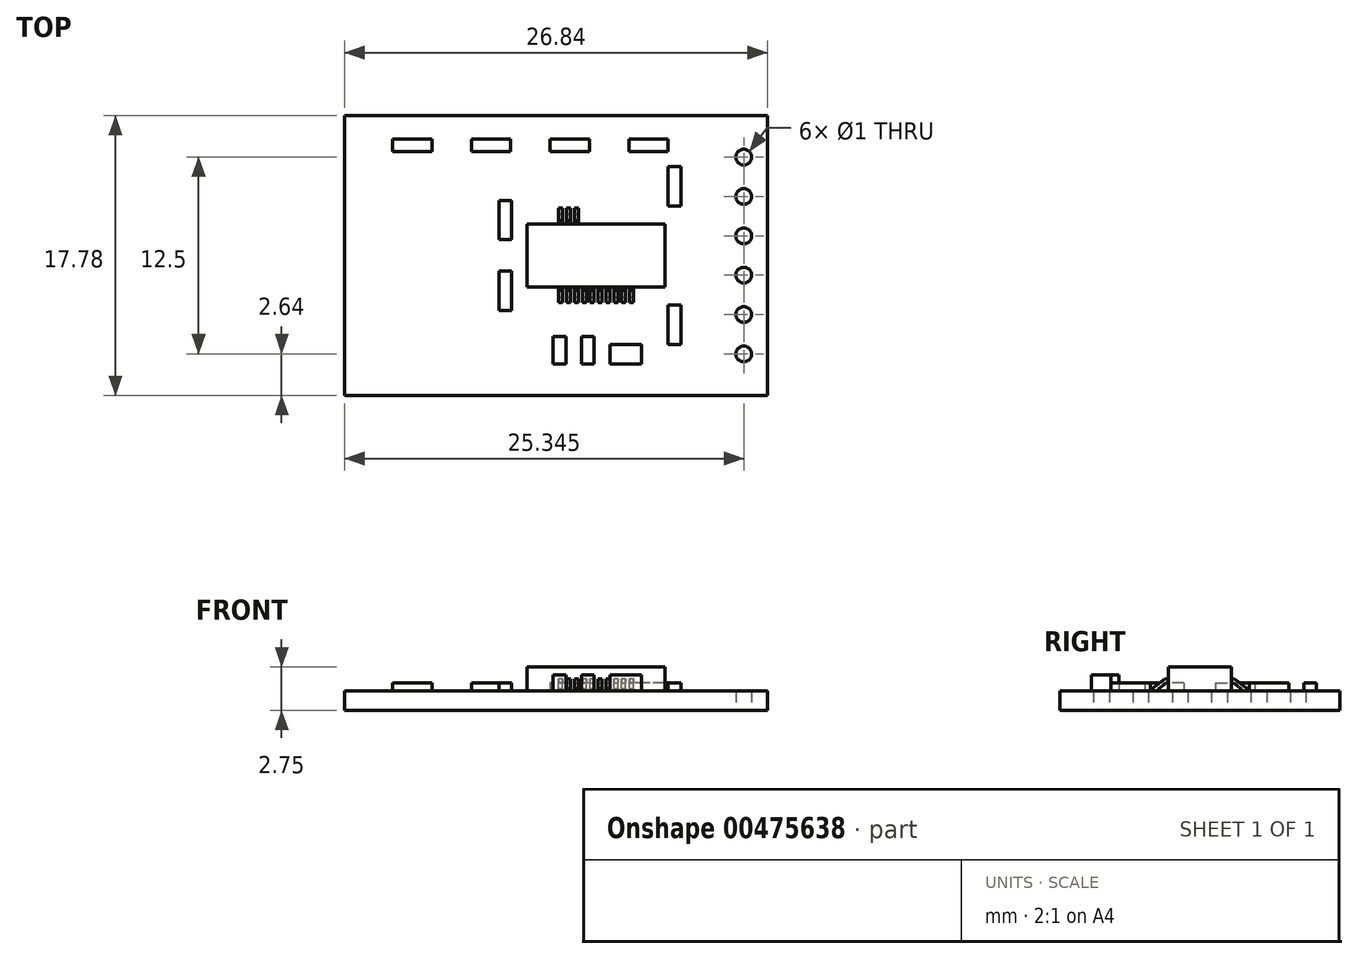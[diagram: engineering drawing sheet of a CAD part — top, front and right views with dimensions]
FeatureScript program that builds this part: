
annotation { "Feature Type Name" : "Feature", "Feature Type Description" : "" }
export const myFeature = defineFeature(function(context is Context, id is Id, definition is map)
    precondition{}
    {
        {
            var Q0;
            Q0=qCreatedBy(makeId("Top.planeOp"),FACE);
            var sketch = newSketch(context, id + "F0", { "sketchPlane" : qUnion([Q0])});
            skLineSegment(sketch, "E0.bottom", {"start": v(13.43, -8.9) * mm, "end": v(-13.42, -8.9) * mm});
            skLineSegment(sketch, "E0.top", {"start": v(13.42, 8.9) * mm, "end": v(-13.43, 8.9) * mm});
            skLineSegment(sketch, "E0.left", {"start": v(13.43, -8.9) * mm, "end": v(13.42, 8.9) * mm});
            skLineSegment(sketch, "E0.right", {"start": v(-13.42, -8.9) * mm, "end": v(-13.43, 8.9) * mm});
            skPoint(sketch, "E0.middle", {"position": v(0, 0) * mm});
            skCircle(sketch, "E1", {"center": v(11.92, 6.25) * mm, "radius": 0.5 * mm});
            skCircle(sketch, "E2.1.0.0", {"center": v(11.92, 3.75) * mm, "radius": 0.5 * mm});
            skCircle(sketch, "E2.2.0.0", {"center": v(11.92, 1.25) * mm, "radius": 0.5 * mm});
            skCircle(sketch, "E2.3.0.0", {"center": v(11.92, -1.25) * mm, "radius": 0.5 * mm});
            skCircle(sketch, "E2.4.0.0", {"center": v(11.92, -3.75) * mm, "radius": 0.5 * mm});
            skCircle(sketch, "E2.5.0.0", {"center": v(11.92, -6.25) * mm, "radius": 0.5 * mm});
            skLineSegment(sketch, "E2.direction1", {"start": v(11.92, 6.25) * mm, "end": v(11.92, 3.75) * mm, "construction": true});
            skLineSegment(sketch, "E3", {"start": v(11.92, 1.25) * mm, "end": v(11.92, -1.25) * mm, "construction": true});
            skPoint(sketch, "E4", {"position": v(11.92, 0) * mm});
            skPoint(sketch, "E5", {"position": v(13.42, 0) * mm});
            skSolve(sketch);
        }
        {
            var Q0;
            Q0 = qSketchRegion(id + "F0", true);
            extrude(context, id + "F1", {"entities" : qUnion([Q0]), "depth" : 1.25 * mm});
        }
        {
            var Q0;
            Q0=makeQuery(id+"F1.opExtrude","CAP_FACE",FACE,{"disambiguationData":[OSD([sQuery(id+"F0.wireOp",EDGE,"E0.bottom"),sQuery(id+"F0.wireOp",EDGE,"E0.top"),sQuery(id+"F0.wireOp",EDGE,"E0.left"),sQuery(id+"F0.wireOp",EDGE,"E0.right"),sQuery(id+"F0.wireOp",EDGE,"E1"),sQuery(id+"F0.wireOp",EDGE,"E2.1.0.0"),sQuery(id+"F0.wireOp",EDGE,"E2.2.0.0"),sQuery(id+"F0.wireOp",EDGE,"E2.3.0.0"),sQuery(id+"F0.wireOp",EDGE,"E2.4.0.0"),sQuery(id+"F0.wireOp",EDGE,"E2.5.0.0")])],"isStart":false});
            var sketch = newSketch(context, id + "F2", { "sketchPlane" : qUnion([Q0])});
            skLineSegment(sketch, "E6.bottom", {"start": v(6.92, -2) * mm, "end": v(-1.83, -2) * mm});
            skLineSegment(sketch, "E6.top", {"start": v(6.92, 2) * mm, "end": v(-1.83, 2) * mm});
            skLineSegment(sketch, "E6.left", {"start": v(6.92, -2) * mm, "end": v(6.92, 2) * mm});
            skLineSegment(sketch, "E6.right", {"start": v(-1.83, -2) * mm, "end": v(-1.83, 2) * mm});
            skPoint(sketch, "E6.middle", {"position": v(2.55, 0) * mm});
            skLineSegment(sketch, "E7.bottom", {"start": v(0.42, -3) * mm, "end": v(0.17, -3) * mm});
            skLineSegment(sketch, "E7.top", {"start": v(0.42, -2) * mm, "end": v(0.17, -2) * mm});
            skLineSegment(sketch, "E7.left", {"start": v(0.42, -3) * mm, "end": v(0.42, -2) * mm});
            skLineSegment(sketch, "E7.right", {"start": v(0.17, -3) * mm, "end": v(0.17, -2) * mm});
            skPoint(sketch, "E7.middle", {"position": v(0.3, -2.5) * mm});
            skPoint(sketch, "E8.1.0.0", {"position": v(0.8, -2.5) * mm});
            skLineSegment(sketch, "E8.1.0.1", {"start": v(0.92, -3) * mm, "end": v(0.67, -3) * mm});
            skLineSegment(sketch, "E8.1.0.2", {"start": v(0.92, -2) * mm, "end": v(0.67, -2) * mm});
            skLineSegment(sketch, "E8.1.0.3", {"start": v(0.92, -3) * mm, "end": v(0.92, -2) * mm});
            skLineSegment(sketch, "E8.1.0.4", {"start": v(0.67, -3) * mm, "end": v(0.67, -2) * mm});
            skPoint(sketch, "E8.2.0.0", {"position": v(1.3, -2.5) * mm});
            skLineSegment(sketch, "E8.2.0.1", {"start": v(1.42, -3) * mm, "end": v(1.17, -3) * mm});
            skLineSegment(sketch, "E8.2.0.2", {"start": v(1.42, -2) * mm, "end": v(1.17, -2) * mm});
            skLineSegment(sketch, "E8.2.0.3", {"start": v(1.42, -3) * mm, "end": v(1.42, -2) * mm});
            skLineSegment(sketch, "E8.2.0.4", {"start": v(1.17, -3) * mm, "end": v(1.17, -2) * mm});
            skPoint(sketch, "E8.3.0.0", {"position": v(1.8, -2.5) * mm});
            skLineSegment(sketch, "E8.3.0.1", {"start": v(1.92, -3) * mm, "end": v(1.67, -3) * mm});
            skLineSegment(sketch, "E8.3.0.2", {"start": v(1.92, -2) * mm, "end": v(1.67, -2) * mm});
            skLineSegment(sketch, "E8.3.0.3", {"start": v(1.92, -3) * mm, "end": v(1.92, -2) * mm});
            skLineSegment(sketch, "E8.3.0.4", {"start": v(1.67, -3) * mm, "end": v(1.67, -2) * mm});
            skPoint(sketch, "E8.4.0.0", {"position": v(2.3, -2.5) * mm});
            skLineSegment(sketch, "E8.4.0.1", {"start": v(2.42, -3) * mm, "end": v(2.17, -3) * mm});
            skLineSegment(sketch, "E8.4.0.2", {"start": v(2.42, -2) * mm, "end": v(2.17, -2) * mm});
            skLineSegment(sketch, "E8.4.0.3", {"start": v(2.42, -3) * mm, "end": v(2.42, -2) * mm});
            skLineSegment(sketch, "E8.4.0.4", {"start": v(2.17, -3) * mm, "end": v(2.17, -2) * mm});
            skPoint(sketch, "E8.5.0.0", {"position": v(2.8, -2.5) * mm});
            skLineSegment(sketch, "E8.5.0.1", {"start": v(2.92, -3) * mm, "end": v(2.67, -3) * mm});
            skLineSegment(sketch, "E8.5.0.2", {"start": v(2.92, -2) * mm, "end": v(2.67, -2) * mm});
            skLineSegment(sketch, "E8.5.0.3", {"start": v(2.92, -3) * mm, "end": v(2.92, -2) * mm});
            skLineSegment(sketch, "E8.5.0.4", {"start": v(2.67, -3) * mm, "end": v(2.67, -2) * mm});
            skPoint(sketch, "E8.6.0.0", {"position": v(3.3, -2.5) * mm});
            skLineSegment(sketch, "E8.6.0.1", {"start": v(3.42, -3) * mm, "end": v(3.17, -3) * mm});
            skLineSegment(sketch, "E8.6.0.2", {"start": v(3.42, -2) * mm, "end": v(3.17, -2) * mm});
            skLineSegment(sketch, "E8.6.0.3", {"start": v(3.42, -3) * mm, "end": v(3.42, -2) * mm});
            skLineSegment(sketch, "E8.6.0.4", {"start": v(3.17, -3) * mm, "end": v(3.17, -2) * mm});
            skPoint(sketch, "E8.7.0.0", {"position": v(3.8, -2.5) * mm});
            skLineSegment(sketch, "E8.7.0.1", {"start": v(3.92, -3) * mm, "end": v(3.67, -3) * mm});
            skLineSegment(sketch, "E8.7.0.2", {"start": v(3.92, -2) * mm, "end": v(3.67, -2) * mm});
            skLineSegment(sketch, "E8.7.0.3", {"start": v(3.92, -3) * mm, "end": v(3.92, -2) * mm});
            skLineSegment(sketch, "E8.7.0.4", {"start": v(3.67, -3) * mm, "end": v(3.67, -2) * mm});
            skPoint(sketch, "E8.8.0.0", {"position": v(4.3, -2.5) * mm});
            skLineSegment(sketch, "E8.8.0.1", {"start": v(4.42, -3) * mm, "end": v(4.17, -3) * mm});
            skLineSegment(sketch, "E8.8.0.2", {"start": v(4.42, -2) * mm, "end": v(4.17, -2) * mm});
            skLineSegment(sketch, "E8.8.0.3", {"start": v(4.42, -3) * mm, "end": v(4.42, -2) * mm});
            skLineSegment(sketch, "E8.8.0.4", {"start": v(4.17, -3) * mm, "end": v(4.17, -2) * mm});
            skPoint(sketch, "E8.9.0.0", {"position": v(4.8, -2.5) * mm});
            skLineSegment(sketch, "E8.9.0.1", {"start": v(4.92, -3) * mm, "end": v(4.67, -3) * mm});
            skLineSegment(sketch, "E8.9.0.2", {"start": v(4.92, -2) * mm, "end": v(4.67, -2) * mm});
            skLineSegment(sketch, "E8.9.0.3", {"start": v(4.92, -3) * mm, "end": v(4.92, -2) * mm});
            skLineSegment(sketch, "E8.9.0.4", {"start": v(4.67, -3) * mm, "end": v(4.67, -2) * mm});
            skLineSegment(sketch, "E8.direction1", {"start": v(0.17, -3) * mm, "end": v(0.67, -3) * mm, "construction": true});
            skLineSegment(sketch, "E9", {"start": v(2.3, -2.5) * mm, "end": v(2.8, -2.5) * mm, "construction": true});
            skPoint(sketch, "E10", {"position": v(2.55, -2.5) * mm});
            skLineSegment(sketch, "E11", {"start": v(-1.83, 0) * mm, "end": v(6.92, 0) * mm, "construction": true});
            skLineSegment(sketch, "E12.MirrorCS", {"start": v(0.42, 3) * mm, "end": v(0.17, 3) * mm});
            skLineSegment(sketch, "E13.MirrorCS", {"start": v(2.92, 2) * mm, "end": v(2.67, 2) * mm});
            skLineSegment(sketch, "E14.MirrorCS", {"start": v(0.42, 2) * mm, "end": v(0.17, 2) * mm});
            skLineSegment(sketch, "E15.MirrorCS", {"start": v(4.92, 2) * mm, "end": v(4.67, 2) * mm});
            skLineSegment(sketch, "E16.MirrorCS", {"start": v(0.92, 3) * mm, "end": v(0.67, 3) * mm});
            skLineSegment(sketch, "E17.MirrorCS", {"start": v(0.92, 2) * mm, "end": v(0.67, 2) * mm});
            skLineSegment(sketch, "E18.MirrorCS", {"start": v(4.42, 2) * mm, "end": v(4.17, 2) * mm});
            skLineSegment(sketch, "E19.MirrorCS", {"start": v(1.42, 3) * mm, "end": v(1.17, 3) * mm});
            skLineSegment(sketch, "E20.MirrorCS", {"start": v(2.42, 2) * mm, "end": v(2.17, 2) * mm});
            skLineSegment(sketch, "E21.MirrorCS", {"start": v(3.92, 2) * mm, "end": v(3.67, 2) * mm});
            skLineSegment(sketch, "E22.MirrorCS", {"start": v(1.92, 2) * mm, "end": v(1.67, 2) * mm});
            skLineSegment(sketch, "E23.MirrorCS", {"start": v(3.92, 3) * mm, "end": v(3.67, 3) * mm});
            skLineSegment(sketch, "E24.MirrorCS", {"start": v(1.92, 3) * mm, "end": v(1.67, 3) * mm});
            skLineSegment(sketch, "E25.MirrorCS", {"start": v(4.42, 3) * mm, "end": v(4.17, 3) * mm});
            skLineSegment(sketch, "E26.MirrorCS", {"start": v(3.42, 2) * mm, "end": v(3.17, 2) * mm});
            skLineSegment(sketch, "E27.MirrorCS", {"start": v(2.42, 3) * mm, "end": v(2.17, 3) * mm});
            skLineSegment(sketch, "E28.MirrorCS", {"start": v(1.42, 2) * mm, "end": v(1.17, 2) * mm});
            skLineSegment(sketch, "E29.MirrorCS", {"start": v(4.92, 3) * mm, "end": v(4.67, 3) * mm});
            skLineSegment(sketch, "E30.MirrorCS", {"start": v(2.3, 2.5) * mm, "end": v(2.8, 2.5) * mm, "construction": true});
            skLineSegment(sketch, "E31.MirrorCS", {"start": v(0.17, 3) * mm, "end": v(0.67, 3) * mm, "construction": true});
            skLineSegment(sketch, "E32.MirrorCS", {"start": v(2.92, 3) * mm, "end": v(2.67, 3) * mm});
            skLineSegment(sketch, "E33.MirrorCS", {"start": v(3.42, 3) * mm, "end": v(3.17, 3) * mm});
            skLineSegment(sketch, "E34.MirrorCS", {"start": v(3.17, 3) * mm, "end": v(3.17, 2) * mm});
            skLineSegment(sketch, "E35.MirrorCS", {"start": v(4.42, 3) * mm, "end": v(4.42, 2) * mm});
            skLineSegment(sketch, "E36.MirrorCS", {"start": v(2.42, 3) * mm, "end": v(2.42, 2) * mm});
            skLineSegment(sketch, "E37.MirrorCS", {"start": v(3.67, 3) * mm, "end": v(3.67, 2) * mm});
            skLineSegment(sketch, "E38.MirrorCS", {"start": v(1.67, 3) * mm, "end": v(1.67, 2) * mm});
            skLineSegment(sketch, "E39.MirrorCS", {"start": v(0.42, 3) * mm, "end": v(0.42, 2) * mm});
            skLineSegment(sketch, "E40.MirrorCS", {"start": v(0.17, 3) * mm, "end": v(0.17, 2) * mm});
            skLineSegment(sketch, "E41.MirrorCS", {"start": v(0.92, 3) * mm, "end": v(0.92, 2) * mm});
            skLineSegment(sketch, "E42.MirrorCS", {"start": v(0.67, 3) * mm, "end": v(0.67, 2) * mm});
            skLineSegment(sketch, "E43.MirrorCS", {"start": v(3.42, 3) * mm, "end": v(3.42, 2) * mm});
            skPoint(sketch, "E44.MirrorP", {"position": v(2.8, 2.5) * mm});
            skLineSegment(sketch, "E45.MirrorCS", {"start": v(3.92, 3) * mm, "end": v(3.92, 2) * mm});
            skPoint(sketch, "E46.MirrorP", {"position": v(0.3, 2.5) * mm});
            skPoint(sketch, "E47.MirrorP", {"position": v(3.8, 2.5) * mm});
            skLineSegment(sketch, "E48.MirrorCS", {"start": v(1.92, 3) * mm, "end": v(1.92, 2) * mm});
            skPoint(sketch, "E49.MirrorP", {"position": v(4.8, 2.5) * mm});
            skPoint(sketch, "E50.MirrorP", {"position": v(1.8, 2.5) * mm});
            skPoint(sketch, "E51.MirrorP", {"position": v(2.55, 2.5) * mm});
            skLineSegment(sketch, "E52.MirrorCS", {"start": v(2.17, 3) * mm, "end": v(2.17, 2) * mm});
            skLineSegment(sketch, "E53.MirrorCS", {"start": v(2.67, 3) * mm, "end": v(2.67, 2) * mm});
            skLineSegment(sketch, "E54.MirrorCS", {"start": v(4.67, 3) * mm, "end": v(4.67, 2) * mm});
            skLineSegment(sketch, "E55.MirrorCS", {"start": v(4.17, 3) * mm, "end": v(4.17, 2) * mm});
            skPoint(sketch, "E56.MirrorP", {"position": v(2.3, 2.5) * mm});
            skPoint(sketch, "E57.MirrorP", {"position": v(3.3, 2.5) * mm});
            skPoint(sketch, "E58.MirrorP", {"position": v(0.8, 2.5) * mm});
            skLineSegment(sketch, "E59.MirrorCS", {"start": v(4.92, 3) * mm, "end": v(4.92, 2) * mm});
            skPoint(sketch, "E60.MirrorP", {"position": v(4.3, 2.5) * mm});
            skLineSegment(sketch, "E61.MirrorCS", {"start": v(2.92, 3) * mm, "end": v(2.92, 2) * mm});
            skPoint(sketch, "E62.MirrorP", {"position": v(1.3, 2.5) * mm});
            skLineSegment(sketch, "E63.MirrorCS", {"start": v(1.17, 3) * mm, "end": v(1.17, 2) * mm});
            skLineSegment(sketch, "E64.MirrorCS", {"start": v(1.42, 3) * mm, "end": v(1.42, 2) * mm});
            skSolve(sketch);
        }
        {
            var Q0;
            {var subQ13=sQuery(id+"F2.wireOp",EDGE,"E6.left");Q0=makeQuery(id+"F2.imprint","IMPRINT",FACE,{"disambiguationData":[TD([[makeQuery(id+"F2.imprint","IMPRINT",EDGE,{"derivedFrom":subQ13}),1.0]])]});}
            extrude(context, id + "F3", {"entities" : qUnion([Q0]), "depth" : 1.5 * mm});
        }
        {
            var Q0;
            Q0=makeQuery(id+"F2.imprint","IMPRINT",FACE,{"disambiguationData":[TD([[makeQuery(id+"F2.imprint","IMPRINT",EDGE,{"derivedFrom":sQuery(id+"F2.wireOp",EDGE,"E15.MirrorCS")}),-1.0]])]});
            var Q1;
            Q1=makeQuery(id+"F2.imprint","IMPRINT",FACE,{"disambiguationData":[TD([[makeQuery(id+"F2.imprint","IMPRINT",EDGE,{"derivedFrom":sQuery(id+"F2.wireOp",EDGE,"E22.MirrorCS")}),-1.0]])]});
            var Q2;
            Q2=makeQuery(id+"F2.imprint","IMPRINT",FACE,{"disambiguationData":[TD([[makeQuery(id+"F2.imprint","IMPRINT",EDGE,{"derivedFrom":sQuery(id+"F2.wireOp",EDGE,"E18.MirrorCS")}),-1.0]])]});
            var Q3;
            Q3=makeQuery(id+"F2.imprint","IMPRINT",FACE,{"disambiguationData":[TD([[makeQuery(id+"F2.imprint","IMPRINT",EDGE,{"derivedFrom":sQuery(id+"F2.wireOp",EDGE,"E8.8.0.1")}),-1.0]])]});
            var Q4;
            Q4=makeQuery(id+"F2.imprint","IMPRINT",FACE,{"disambiguationData":[TD([[makeQuery(id+"F2.imprint","IMPRINT",EDGE,{"derivedFrom":sQuery(id+"F2.wireOp",EDGE,"E13.MirrorCS")}),-1.0]])]});
            var Q5;
            Q5=makeQuery(id+"F2.imprint","IMPRINT",FACE,{"disambiguationData":[TD([[makeQuery(id+"F2.imprint","IMPRINT",EDGE,{"derivedFrom":sQuery(id+"F2.wireOp",EDGE,"E19.MirrorCS")}),1.0]])]});
            var Q6;
            Q6=makeQuery(id+"F2.imprint","IMPRINT",FACE,{"disambiguationData":[TD([[makeQuery(id+"F2.imprint","IMPRINT",EDGE,{"derivedFrom":sQuery(id+"F2.wireOp",EDGE,"E8.9.0.1")}),-1.0]])]});
            var Q7;
            Q7=makeQuery(id+"F2.imprint","IMPRINT",FACE,{"disambiguationData":[TD([[makeQuery(id+"F2.imprint","IMPRINT",EDGE,{"derivedFrom":sQuery(id+"F2.wireOp",EDGE,"E26.MirrorCS")}),-1.0]])]});
            var Q8;
            Q8=makeQuery(id+"F2.imprint","IMPRINT",FACE,{"disambiguationData":[TD([[makeQuery(id+"F2.imprint","IMPRINT",EDGE,{"derivedFrom":sQuery(id+"F2.wireOp",EDGE,"E8.2.0.1")}),-1.0]])]});
            var Q9;
            Q9=makeQuery(id+"F2.imprint","IMPRINT",FACE,{"disambiguationData":[TD([[makeQuery(id+"F2.imprint","IMPRINT",EDGE,{"derivedFrom":sQuery(id+"F2.wireOp",EDGE,"E7.bottom")}),-1.0]])]});
            var Q10;
            Q10=makeQuery(id+"F2.imprint","IMPRINT",FACE,{"disambiguationData":[TD([[makeQuery(id+"F2.imprint","IMPRINT",EDGE,{"derivedFrom":sQuery(id+"F2.wireOp",EDGE,"E8.3.0.1")}),-1.0]])]});
            var Q11;
            Q11=makeQuery(id+"F2.imprint","IMPRINT",FACE,{"disambiguationData":[TD([[makeQuery(id+"F2.imprint","IMPRINT",EDGE,{"derivedFrom":sQuery(id+"F2.wireOp",EDGE,"E8.4.0.1")}),-1.0]])]});
            var Q12;
            Q12=makeQuery(id+"F2.imprint","IMPRINT",FACE,{"disambiguationData":[TD([[makeQuery(id+"F2.imprint","IMPRINT",EDGE,{"derivedFrom":sQuery(id+"F2.wireOp",EDGE,"E8.5.0.1")}),-1.0]])]});
            var Q13;
            Q13=makeQuery(id+"F2.imprint","IMPRINT",FACE,{"disambiguationData":[TD([[makeQuery(id+"F2.imprint","IMPRINT",EDGE,{"derivedFrom":sQuery(id+"F2.wireOp",EDGE,"E8.6.0.1")}),-1.0]])]});
            var Q14;
            Q14=makeQuery(id+"F2.imprint","IMPRINT",FACE,{"disambiguationData":[TD([[makeQuery(id+"F2.imprint","IMPRINT",EDGE,{"derivedFrom":sQuery(id+"F2.wireOp",EDGE,"E12.MirrorCS")}),1.0]])]});
            var Q15;
            Q15=makeQuery(id+"F2.imprint","IMPRINT",FACE,{"disambiguationData":[TD([[makeQuery(id+"F2.imprint","IMPRINT",EDGE,{"derivedFrom":sQuery(id+"F2.wireOp",EDGE,"E20.MirrorCS")}),-1.0]])]});
            var Q16;
            Q16=makeQuery(id+"F2.imprint","IMPRINT",FACE,{"disambiguationData":[TD([[makeQuery(id+"F2.imprint","IMPRINT",EDGE,{"derivedFrom":sQuery(id+"F2.wireOp",EDGE,"E21.MirrorCS")}),-1.0]])]});
            var Q17;
            Q17=makeQuery(id+"F2.imprint","IMPRINT",FACE,{"disambiguationData":[TD([[makeQuery(id+"F2.imprint","IMPRINT",EDGE,{"derivedFrom":sQuery(id+"F2.wireOp",EDGE,"E16.MirrorCS")}),1.0]])]});
            var Q18;
            Q18=makeQuery(id+"F2.imprint","IMPRINT",FACE,{"disambiguationData":[TD([[makeQuery(id+"F2.imprint","IMPRINT",EDGE,{"derivedFrom":sQuery(id+"F2.wireOp",EDGE,"E8.7.0.1")}),-1.0]])]});
            var Q19;
            Q19=makeQuery(id+"F2.imprint","IMPRINT",FACE,{"disambiguationData":[TD([[makeQuery(id+"F2.imprint","IMPRINT",EDGE,{"derivedFrom":sQuery(id+"F2.wireOp",EDGE,"E8.1.0.1")}),-1.0]])]});
            extrude(context, id + "F4", {"entities" : qUnion([Q0, Q1, Q2, Q3, Q4, Q5, Q6, Q7, Q8, Q9, Q10, Q11, Q12, Q13, Q14, Q15, Q16, Q17, Q18, Q19]), "depth" : .75 * mm});
        }
        {
            var Q0;
            Q0=qCreatedBy(makeId("Right.planeOp"),FACE);
            var sketch = newSketch(context, id + "F5", { "sketchPlane" : qUnion([Q0])});
            skLineSegment(sketch, "E65", {"start": v(0, -0.74) * mm, "end": v(0, 2.74) * mm, "construction": true});
            skLineSegment(sketch, "E66", {"start": v(-2, 1.75) * mm, "end": v(-2.12, 1.75) * mm});
            skLineSegment(sketch, "E67", {"start": v(-2.12, 1.75) * mm, "end": v(-2.63, 1.38) * mm});
            skLineSegment(sketch, "E68", {"start": v(-2.63, 1.38) * mm, "end": v(-2.63, 1.25) * mm});
            skLineSegment(sketch, "E69", {"start": v(-2.63, 1.25) * mm, "end": v(-2, 1.25) * mm});
            skLineSegment(sketch, "E70", {"start": v(-2, 1.25) * mm, "end": v(-2, 1.75) * mm});
            skLineSegment(sketch, "E71", {"start": v(-3, 1.25) * mm, "end": v(-2, 2) * mm, "construction": true});
            skLineSegment(sketch, "E72", {"start": v(-2.2, 2) * mm, "end": v(-3, 1.4) * mm});
            skLineSegment(sketch, "E73", {"start": v(-3, 1.4) * mm, "end": v(-3, 2) * mm});
            skLineSegment(sketch, "E74", {"start": v(-3, 2) * mm, "end": v(-2.2, 2) * mm});
            skLineSegment(sketch, "E75.MirrorCS", {"start": v(2, 1.75) * mm, "end": v(2.12, 1.75) * mm});
            skLineSegment(sketch, "E76.MirrorCS", {"start": v(2, 1.25) * mm, "end": v(2, 1.75) * mm});
            skLineSegment(sketch, "E77.MirrorCS", {"start": v(2.12, 1.75) * mm, "end": v(2.63, 1.38) * mm});
            skLineSegment(sketch, "E78.MirrorCS", {"start": v(2.63, 1.25) * mm, "end": v(2, 1.25) * mm});
            skLineSegment(sketch, "E79.MirrorCS", {"start": v(2.63, 1.38) * mm, "end": v(2.63, 1.25) * mm});
            skLineSegment(sketch, "E80.MirrorCS", {"start": v(2.2, 2) * mm, "end": v(3, 1.4) * mm});
            skLineSegment(sketch, "E81.MirrorCS", {"start": v(3, 2) * mm, "end": v(2.2, 2) * mm});
            skLineSegment(sketch, "E82.MirrorCS", {"start": v(3, 1.4) * mm, "end": v(3, 2) * mm});
            skSolve(sketch);
        }
        {
            var Q0;
            Q0 = qSketchRegion(id + "F5", true);
            extrude(context, id + "F6", {"entities" : qUnion([Q0]), "operationType" : NewBodyOperationType.REMOVE, "endBound" : BoundingType.THROUGH_ALL, "oppositeDirection" : true, "depth" : 25.4 * mm, "hasSecondDirection" : true, "secondDirectionOppositeDirection" : false, "secondDirectionDepth" : 25.4 * mm});
        }
        {
            var Q0;
            {var subQ12=sQuery(id+"F2.wireOp",EDGE,"E6.left");Q0=makeQuery(id+"F2.imprint","IMPRINT",FACE,{"disambiguationData":[TD([[makeQuery(id+"F2.imprint","IMPRINT",EDGE,{"derivedFrom":subQ12}),-1.0]])]});}
            var sketch = newSketch(context, id + "F7", { "sketchPlane" : qUnion([Q0])});
            skLineSegment(sketch, "E83.bottom", {"start": v(7.92, 3.15) * mm, "end": v(7.12, 3.15) * mm});
            skLineSegment(sketch, "E83.top", {"start": v(7.92, 5.65) * mm, "end": v(7.12, 5.65) * mm});
            skLineSegment(sketch, "E83.left", {"start": v(7.92, 3.15) * mm, "end": v(7.92, 5.65) * mm});
            skLineSegment(sketch, "E83.right", {"start": v(7.12, 3.15) * mm, "end": v(7.12, 5.65) * mm});
            skPoint(sketch, "E83.middle", {"position": v(7.52, 4.4) * mm});
            skLineSegment(sketch, "E84", {"start": v(13.42, 0) * mm, "end": v(-13.42, 0) * mm, "construction": true});
            skLineSegment(sketch, "E85.MirrorCS", {"start": v(7.92, -3.15) * mm, "end": v(7.12, -3.15) * mm});
            skLineSegment(sketch, "E86.MirrorCS", {"start": v(7.12, -3.15) * mm, "end": v(7.12, -5.65) * mm});
            skLineSegment(sketch, "E87.MirrorCS", {"start": v(7.92, -5.65) * mm, "end": v(7.12, -5.65) * mm});
            skLineSegment(sketch, "E88.MirrorCS", {"start": v(7.92, -3.15) * mm, "end": v(7.92, -5.65) * mm});
            skLineSegment(sketch, "E89.bottom", {"start": v(7.12, 6.6) * mm, "end": v(4.62, 6.6) * mm});
            skLineSegment(sketch, "E89.top", {"start": v(7.12, 7.4) * mm, "end": v(4.62, 7.4) * mm});
            skLineSegment(sketch, "E89.left", {"start": v(7.12, 6.6) * mm, "end": v(7.12, 7.4) * mm});
            skLineSegment(sketch, "E89.right", {"start": v(4.62, 6.6) * mm, "end": v(4.62, 7.4) * mm});
            skPoint(sketch, "E89.middle", {"position": v(5.87, 7) * mm});
            skLineSegment(sketch, "E90.bottom", {"start": v(-2.83, 1) * mm, "end": v(-3.63, 1) * mm});
            skLineSegment(sketch, "E90.top", {"start": v(-2.83, 3.5) * mm, "end": v(-3.63, 3.5) * mm});
            skLineSegment(sketch, "E90.left", {"start": v(-2.83, 1) * mm, "end": v(-2.83, 3.5) * mm});
            skLineSegment(sketch, "E90.right", {"start": v(-3.63, 1) * mm, "end": v(-3.63, 3.5) * mm});
            skPoint(sketch, "E90.middle", {"position": v(-3.23, 2.25) * mm});
            skLineSegment(sketch, "E91.MirrorCS", {"start": v(-3.63, -1) * mm, "end": v(-3.63, -3.5) * mm});
            skPoint(sketch, "E92.MirrorP", {"position": v(-3.23, -2.25) * mm});
            skLineSegment(sketch, "E93.MirrorCS", {"start": v(-2.83, -3.5) * mm, "end": v(-3.63, -3.5) * mm});
            skLineSegment(sketch, "E94.MirrorCS", {"start": v(-2.83, -1) * mm, "end": v(-3.63, -1) * mm});
            skLineSegment(sketch, "E95.MirrorCS", {"start": v(-2.83, -1) * mm, "end": v(-2.83, -3.5) * mm});
            skLineSegment(sketch, "E96.1.0.0", {"start": v(2.12, 7.4) * mm, "end": v(-0.38, 7.4) * mm});
            skLineSegment(sketch, "E96.1.0.1", {"start": v(2.12, 6.6) * mm, "end": v(2.12, 7.4) * mm});
            skPoint(sketch, "E96.1.0.2", {"position": v(0.87, 7) * mm});
            skLineSegment(sketch, "E96.1.0.3", {"start": v(-0.38, 6.6) * mm, "end": v(-0.38, 7.4) * mm});
            skLineSegment(sketch, "E96.1.0.4", {"start": v(2.12, 6.6) * mm, "end": v(-0.38, 6.6) * mm});
            skLineSegment(sketch, "E96.2.0.0", {"start": v(-2.88, 7.4) * mm, "end": v(-5.38, 7.4) * mm});
            skLineSegment(sketch, "E96.2.0.1", {"start": v(-2.88, 6.6) * mm, "end": v(-2.88, 7.4) * mm});
            skPoint(sketch, "E96.2.0.2", {"position": v(-4.12, 7) * mm});
            skLineSegment(sketch, "E96.2.0.3", {"start": v(-5.38, 6.6) * mm, "end": v(-5.38, 7.4) * mm});
            skLineSegment(sketch, "E96.2.0.4", {"start": v(-2.88, 6.6) * mm, "end": v(-5.38, 6.6) * mm});
            skLineSegment(sketch, "E96.3.0.0", {"start": v(-7.88, 7.4) * mm, "end": v(-10.38, 7.4) * mm});
            skLineSegment(sketch, "E96.3.0.1", {"start": v(-7.88, 6.6) * mm, "end": v(-7.88, 7.4) * mm});
            skPoint(sketch, "E96.3.0.2", {"position": v(-9.12, 7) * mm});
            skLineSegment(sketch, "E96.3.0.3", {"start": v(-10.37, 6.6) * mm, "end": v(-10.37, 7.4) * mm});
            skLineSegment(sketch, "E96.3.0.4", {"start": v(-7.88, 6.6) * mm, "end": v(-10.37, 6.6) * mm});
            skLineSegment(sketch, "E96.direction1", {"start": v(4.62, 6.6) * mm, "end": v(-0.38, 6.6) * mm, "construction": true});
            skSolve(sketch);
        }
        {
            var Q0;
            Q0 = qSketchRegion(id + "F7", true);
            extrude(context, id + "F8", {"entities" : qUnion([Q0]), "depth" : .5 * mm});
        }
        {
            var Q0;
            {var subQ12=sQuery(id+"F2.wireOp",EDGE,"E6.left");Q0=makeQuery(id+"F2.imprint","IMPRINT",FACE,{"disambiguationData":[TD([[makeQuery(id+"F2.imprint","IMPRINT",EDGE,{"derivedFrom":subQ12}),-1.0]])]});}
            var sketch = newSketch(context, id + "F9", { "sketchPlane" : qUnion([Q0])});
            skLineSegment(sketch, "E97.bottom", {"start": v(0.63, -6.9) * mm, "end": v(-0.17, -6.9) * mm});
            skLineSegment(sketch, "E97.top", {"start": v(0.63, -5.14) * mm, "end": v(-0.17, -5.14) * mm});
            skLineSegment(sketch, "E97.left", {"start": v(0.63, -6.9) * mm, "end": v(0.63, -5.14) * mm});
            skLineSegment(sketch, "E97.right", {"start": v(-0.17, -6.9) * mm, "end": v(-0.17, -5.14) * mm});
            skPoint(sketch, "E97.middle", {"position": v(0.23, -6.02) * mm});
            skLineSegment(sketch, "E98.bottom", {"start": v(2.43, -6.9) * mm, "end": v(1.63, -6.9) * mm});
            skLineSegment(sketch, "E98.top", {"start": v(2.43, -5.14) * mm, "end": v(1.63, -5.14) * mm});
            skLineSegment(sketch, "E98.left", {"start": v(2.43, -6.9) * mm, "end": v(2.43, -5.14) * mm});
            skLineSegment(sketch, "E98.right", {"start": v(1.63, -6.9) * mm, "end": v(1.63, -5.14) * mm});
            skPoint(sketch, "E98.middle", {"position": v(2.03, -6.02) * mm});
            skPoint(sketch, "E98.middle.positionSnap0", {"position": v(0.63, -6.02) * mm});
            skPoint(sketch, "E98.centerSnap0", {"position": v(0.63, -6.02) * mm});
            skLineSegment(sketch, "E99.bottom", {"start": v(5.43, -6.9) * mm, "end": v(3.43, -6.9) * mm});
            skLineSegment(sketch, "E99.top", {"start": v(5.43, -5.64) * mm, "end": v(3.43, -5.64) * mm});
            skLineSegment(sketch, "E99.left", {"start": v(5.43, -6.9) * mm, "end": v(5.43, -5.64) * mm});
            skLineSegment(sketch, "E99.right", {"start": v(3.43, -6.9) * mm, "end": v(3.43, -5.64) * mm});
            skPoint(sketch, "E99.middle", {"position": v(4.43, -6.27) * mm});
            skSolve(sketch);
        }
        {
            var Q0;
            Q0 = qSketchRegion(id + "F9", true);
            extrude(context, id + "F10", {"entities" : qUnion([Q0]), "depth" : 1 * mm});
        }
    });
